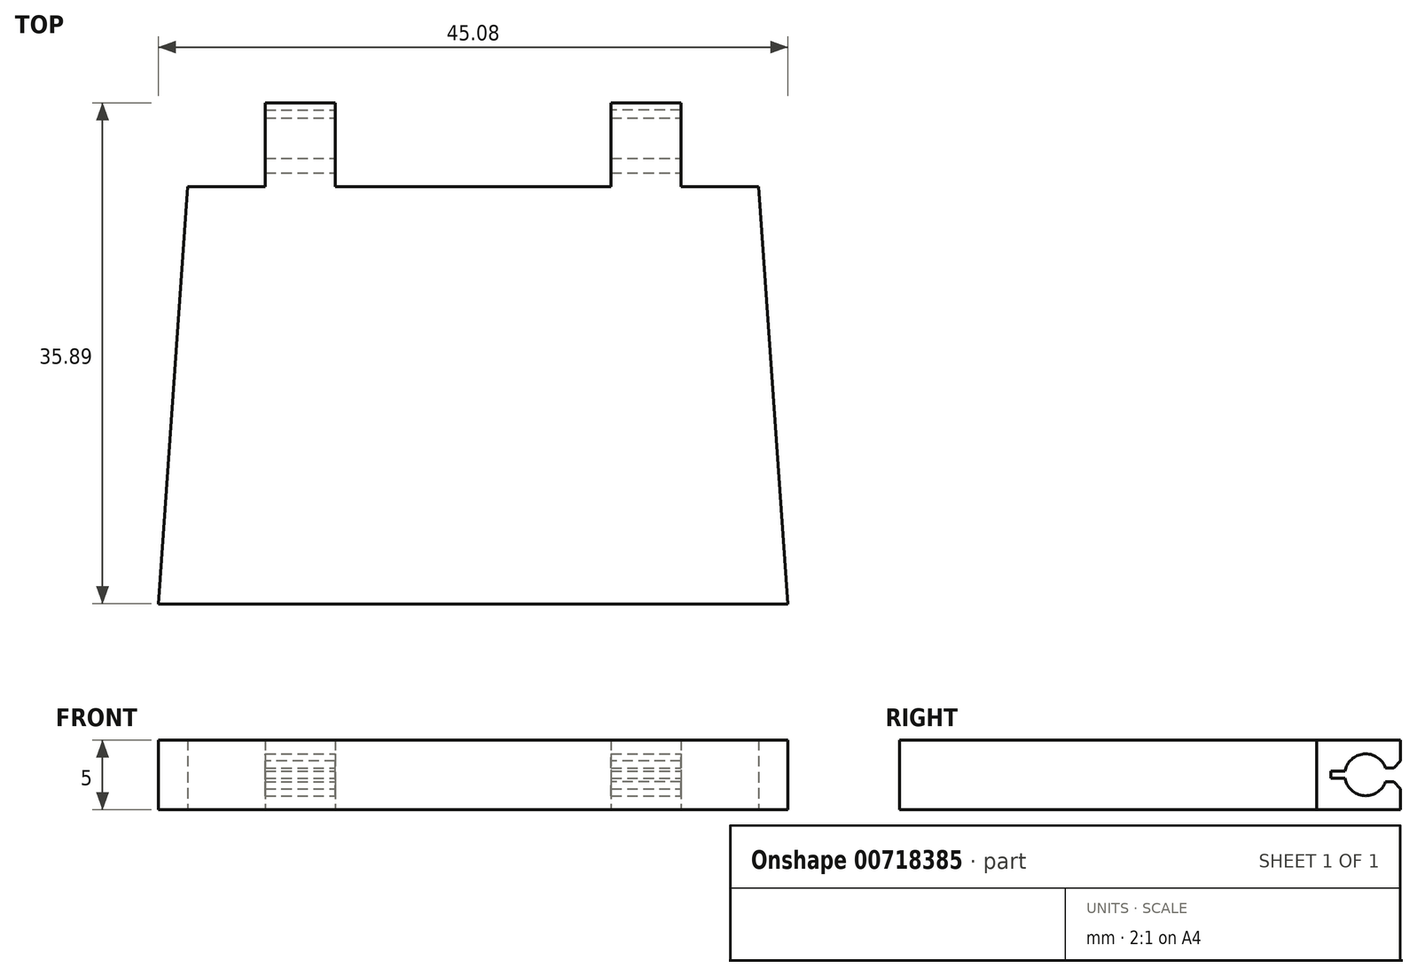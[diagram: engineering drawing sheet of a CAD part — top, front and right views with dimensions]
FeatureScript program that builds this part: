
annotation { "Feature Type Name" : "Feature", "Feature Type Description" : "" }
export const myFeature = defineFeature(function(context is Context, id is Id, definition is map)
    precondition{}
    {
        {
            var Q0;
            Q0=qCreatedBy(makeId("Top.planeOp"),FACE);
            var sketch = newSketch(context, id + "F0", { "sketchPlane" : qUnion([Q0])});
            skLineSegment(sketch, "E0", {"start": v(-20.46, 87.1) * mm, "end": v(-14.89, 87.1) * mm});
            skLineSegment(sketch, "E1.top", {"start": v(-14.89, 93.1) * mm, "end": v(-9.89, 93.1) * mm});
            skLineSegment(sketch, "E1.left", {"start": v(-14.89, 87.1) * mm, "end": v(-14.89, 93.1) * mm});
            skLineSegment(sketch, "E1.right", {"start": v(-9.89, 87.1) * mm, "end": v(-9.89, 93.1) * mm});
            skLineSegment(sketch, "E2.MirrorCS", {"start": v(14.89, 93.1) * mm, "end": v(9.89, 93.1) * mm});
            skLineSegment(sketch, "E3.trimOffspring", {"start": v(-20.46, 87.1) * mm, "end": v(-22.54, 57.2) * mm});
            skLineSegment(sketch, "E4.trimOffspring", {"start": v(14.89, 87.1) * mm, "end": v(20.46, 87.1) * mm});
            skLineSegment(sketch, "E5.trimOffspring", {"start": v(20.46, 87.1) * mm, "end": v(22.54, 57.2) * mm});
            skLineSegment(sketch, "E6.trimOffspring", {"start": v(-9.89, 87.1) * mm, "end": v(9.89, 87.1) * mm});
            skLineSegment(sketch, "E7", {"start": v(9.89, 93.1) * mm, "end": v(9.89, 87.1) * mm});
            skLineSegment(sketch, "E8", {"start": v(14.89, 93.1) * mm, "end": v(14.89, 87.1) * mm});
            skLineSegment(sketch, "E9", {"start": v(-22.54, 57.2) * mm, "end": v(22.54, 57.2) * mm});
            skSolve(sketch);
        }
        {
            var Q0;
            Q0=qSketchRegion(id+"F0",true);
            extrude(context, id + "F1", {"entities" : qUnion([Q0]), "depth" : 5 * mm, "offsetDistance" : 25 * mm});
        }
        {
            var Q0;
            Q0=makeQuery(id+"F1.opExtrude","SWEPT_FACE",FACE,{"disambiguationData":[OSD([sQuery(id+"F0.wireOp",EDGE,"E8")])]});
            cPlane(context, id + "F2", {"entities" : qUnion([Q0]), "cplaneType" : CPlaneType.OFFSET, "offset" : 10 * mm, "width" : 150 * mm, "height" : 150 * mm});
        }
        {
            var Q0;
            Q0=qCreatedBy(id+"F2.planeOp",FACE);
            var sketch = newSketch(context, id + "F3", { "sketchPlane" : qUnion([Q0])});
            skArc(sketch, "E10", {"start": v(92.01, 3) * mm, "mid": v(90.47, 4) * mm, "end": v(89.12, 2.75) * mm});
            skLineSegment(sketch, "E11.bottom", {"start": v(95.6, 3) * mm, "end": v(92.01, 3) * mm});
            skLineSegment(sketch, "E11.top", {"start": v(95.6, 2) * mm, "end": v(92.01, 2) * mm});
            skLineSegment(sketch, "E11.left", {"start": v(95.6, 3) * mm, "end": v(95.6, 2) * mm});
            skPoint(sketch, "E12.orphan", {"position": v(90.6, 2) * mm});
            skLineSegment(sketch, "E13.bottom", {"start": v(89.12, 2.75) * mm, "end": v(88.1, 2.75) * mm});
            skLineSegment(sketch, "E13.top", {"start": v(89.12, 2.25) * mm, "end": v(88.1, 2.25) * mm});
            skLineSegment(sketch, "E13.right", {"start": v(88.1, 2.75) * mm, "end": v(88.1, 2.25) * mm});
            skArc(sketch, "E14.trimOffspring", {"start": v(89.12, 2.25) * mm, "mid": v(90.47, 1) * mm, "end": v(92.01, 2) * mm});
            skSolve(sketch);
        }
        {
            var Q0;
            Q0=qSketchRegion(id+"F3",true);
            extrude(context, id + "F4", {"entities" : qUnion([Q0]), "operationType" : NewBodyOperationType.REMOVE, "oppositeDirection" : true, "depth" : 45.5 * mm, "offsetDistance" : 25 * mm});
        }
        {
            var Q0;
            Q0=makeQuery(id+"F4.boolean.opBoolean","INTERSECT",EDGE,{"derivedFrom":[makeQuery(id+"F1.opExtrude","SWEPT_FACE",FACE,{"disambiguationData":[OSD([sQuery(id+"F0.wireOp",EDGE,"E1.top")])]}),makeQuery(id+"F4.opExtrude","SWEPT_FACE",FACE,{"disambiguationData":[OSD([sQuery(id+"F3.wireOp",EDGE,"E11.bottom")])]})]});
            var Q1;
            Q1=makeQuery(id+"F4.boolean.opBoolean","INTERSECT",EDGE,{"derivedFrom":[makeQuery(id+"F1.opExtrude","SWEPT_FACE",FACE,{"disambiguationData":[OSD([sQuery(id+"F0.wireOp",EDGE,"E1.top")])]}),makeQuery(id+"F4.opExtrude","SWEPT_FACE",FACE,{"disambiguationData":[OSD([sQuery(id+"F3.wireOp",EDGE,"E11.top")])]})]});
            var Q2;
            Q2=makeQuery(id+"F4.boolean.opBoolean","INTERSECT",EDGE,{"derivedFrom":[makeQuery(id+"F1.opExtrude","SWEPT_FACE",FACE,{"disambiguationData":[OSD([sQuery(id+"F0.wireOp",EDGE,"E2.MirrorCS")])]}),makeQuery(id+"F4.opExtrude","SWEPT_FACE",FACE,{"disambiguationData":[OSD([sQuery(id+"F3.wireOp",EDGE,"E11.bottom")])]})]});
            var Q3;
            Q3=makeQuery(id+"F4.boolean.opBoolean","INTERSECT",EDGE,{"derivedFrom":[makeQuery(id+"F1.opExtrude","SWEPT_FACE",FACE,{"disambiguationData":[OSD([sQuery(id+"F0.wireOp",EDGE,"E2.MirrorCS")])]}),makeQuery(id+"F4.opExtrude","SWEPT_FACE",FACE,{"disambiguationData":[OSD([sQuery(id+"F3.wireOp",EDGE,"E11.top")])]})]});
            chamfer(context, id + "F5", {"entities" : qUnion([Q0, Q1, Q2, Q3]), "width" : 0.5 * mm, "tangentPropagation" : true});
        }
    });
